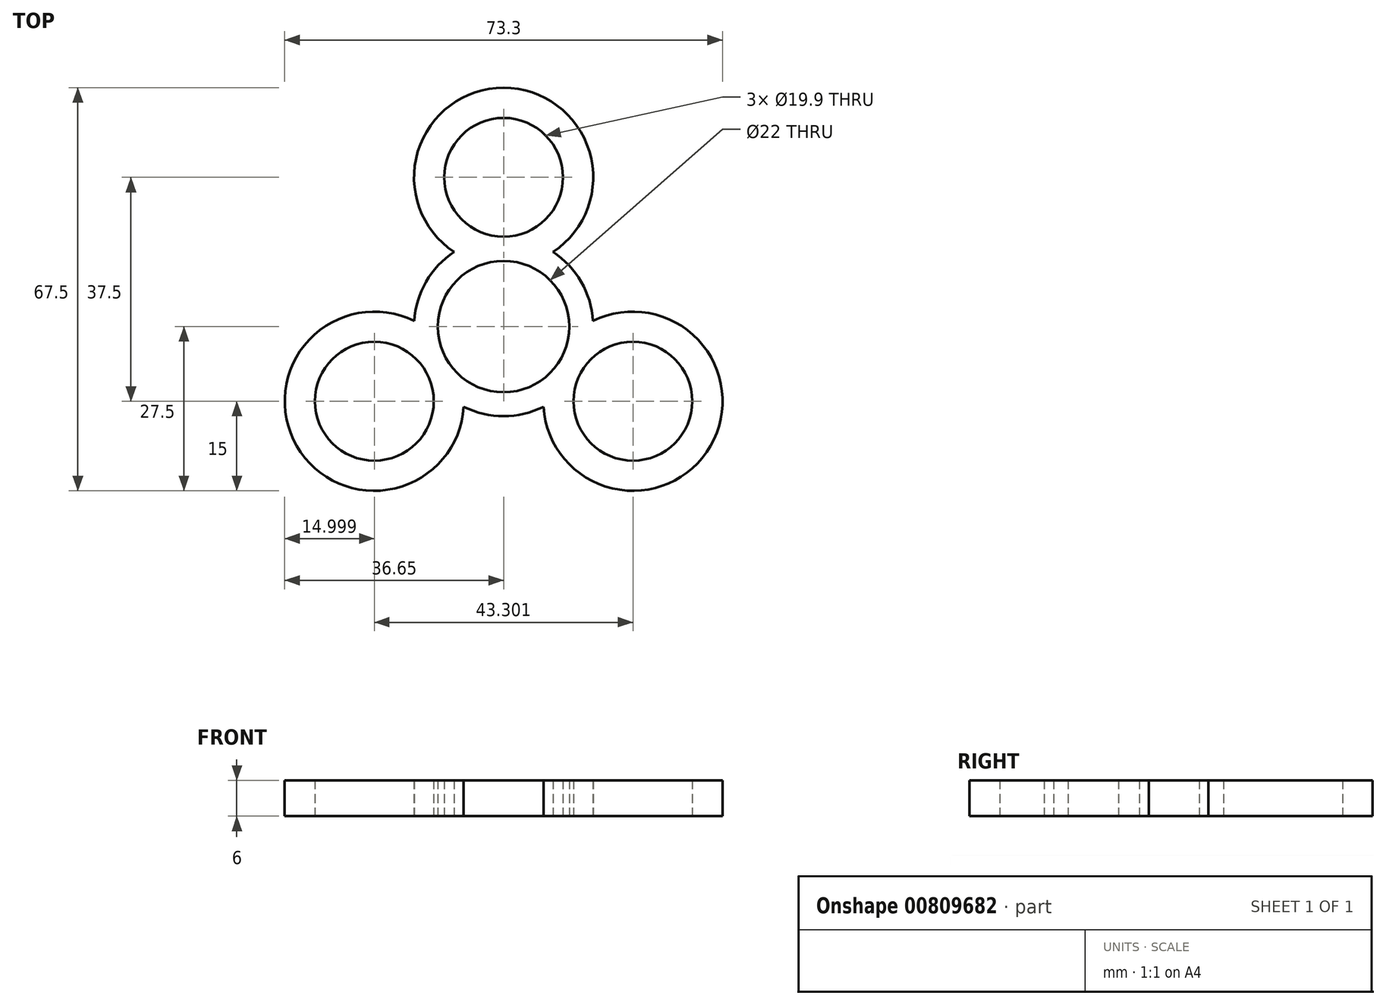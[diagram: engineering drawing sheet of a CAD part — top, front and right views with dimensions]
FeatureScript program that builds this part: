
annotation { "Feature Type Name" : "Feature", "Feature Type Description" : "" }
export const myFeature = defineFeature(function(context is Context, id is Id, definition is map)
    precondition{}
    {
        {
            var Q0;
            Q0=qCreatedBy(makeId("Top.planeOp"),FACE);
            var sketch = newSketch(context, id + "F0", { "sketchPlane" : qUnion([Q0])});
            skArc(sketch, "E0", {"start": v(9.53, 5.5) * mm, "mid": v(0, 11) * mm, "end": v(-9.53, 5.5) * mm});
            skLineSegment(sketch, "E1", {"start": v(0, 0) * mm, "end": v(0, 25) * mm});
            skArc(sketch, "E2", {"start": v(-8.3, 12.5) * mm, "mid": v(-10.93, 10.27) * mm, "end": v(-13, 7.5) * mm});
            skCircle(sketch, "E3", {"center": v(0, 25) * mm, "radius": 9.95 * mm});
            skArc(sketch, "E4", {"start": v(8.3, 12.5) * mm, "mid": v(0, 40) * mm, "end": v(-8.3, 12.5) * mm});
            skArc(sketch, "E5.trimOffspring", {"start": v(13, 7.5) * mm, "mid": v(10.93, 10.27) * mm, "end": v(8.3, 12.5) * mm});
            skArc(sketch, "E6.1.0", {"start": v(-6.68, -13.43) * mm, "mid": v(-3.43, -14.6) * mm, "end": v(0, -15) * mm});
            skArc(sketch, "E6.2.0", {"start": v(14.97, 0.93) * mm, "mid": v(14.36, 4.33) * mm, "end": v(13, 7.5) * mm});
            skArc(sketch, "E7.1.0", {"start": v(-9.53, 5.5) * mm, "mid": v(-9.53, -5.5) * mm, "end": v(0, -11) * mm});
            skArc(sketch, "E7.2.0", {"start": v(0, -11) * mm, "mid": v(9.53, -5.5) * mm, "end": v(9.53, 5.5) * mm});
            skArc(sketch, "E8.1.0", {"start": v(-14.97, 0.93) * mm, "mid": v(-34.64, -20) * mm, "end": v(-6.68, -13.43) * mm});
            skArc(sketch, "E8.2.0", {"start": v(6.68, -13.43) * mm, "mid": v(34.64, -20) * mm, "end": v(14.97, 0.93) * mm});
            skArc(sketch, "E9.1.0", {"start": v(-13, 7.5) * mm, "mid": v(-14.36, 4.33) * mm, "end": v(-14.97, 0.93) * mm});
            skArc(sketch, "E9.2.0", {"start": v(0, -15) * mm, "mid": v(3.43, -14.6) * mm, "end": v(6.68, -13.43) * mm});
            skCircle(sketch, "E10.1.0", {"center": v(-21.65, -12.5) * mm, "radius": 9.95 * mm});
            skCircle(sketch, "E10.2.0", {"center": v(21.65, -12.5) * mm, "radius": 9.95 * mm});
            skSolve(sketch);
        }
        {
            var Q0;
            Q0 = qSketchRegion(id + "F0", true);
            extrude(context, id + "F1", {"entities" : qUnion([Q0]), "depth" : 6 * mm, "offsetDistance" : 25 * mm});
        }
    });
